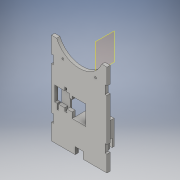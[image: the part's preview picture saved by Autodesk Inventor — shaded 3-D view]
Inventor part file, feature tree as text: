
AUTODESK INVENTOR PART (.ipt)
format: ipt  version: 2016 (Build 200138000, 138)  size: 343,552 bytes
history: native  units: in
note: dims shown in document units (in); Inventor stores cm internally (conversion verified against a paired STEP export)
features: reference x18, extrude x16, sketch x15, plane x2, projected_geometry x1
ambient origin geometry x8: Origin, YZ Plane, XZ Plane, XY Plane, X Axis, Y Axis, Z Axis, Center Point
bodies: Solid1 (feature_tree)
feature tree (52):
  extrude  "Extrusion1"  Depth=0.1969in TaperAngle=0.0deg
  extrude  "Extrusion2"  Depth=0.1969in TaperAngle=0.0deg
  extrude  "Extrusion3"  Depth=0.0787in
  extrude  "Extrusion4"  Depth=0.1969in TaperAngle=0.0deg
  extrude  "Extrusion6"  Depth=0.1969in
  extrude  "Extrusion7"  Depth=0.1969in TaperAngle=0.0deg
  extrude  "Extrusion8"  Depth=0.5in
  plane  "Work Plane1"
  extrude  "Extrusion18"  Depth=0.25in TaperAngle=0.0deg
  extrude  "Extrusion19"  Depth=0.15in
  extrude  "Extrusion21"  Depth=0.1181in
  plane  "Work Plane2"
  extrude  "Extrusion23"  Depth=1.0in TaperAngle=0.0deg
  extrude  "Extrusion24"  Depth=0.325in
  extrude  "Extrusion25"  Depth=0.0197in
  extrude  "Extrusion26"  Depth=0.0197in
  extrude  "Extrusion27"  Depth=1.0in
  extrude  "Extrusion28"  Depth=0.5in
  sketch  "Sketch1"  dims[d0=6.0in d1=0.1969in d2=0.0in]
  sketch  "Sketch2"  dims[d3=0.5906in d4=0.1969in d5=0.0in]
  reference  "Reference2"
  reference  "Reference3"
  sketch  "Sketch4"  dims[d6=3.0in d7=0.0787in]
  sketch  "Sketch6"  dims[d8=0.0787in d9=0.1969in d10=0.0in]
  sketch  "Sketch7"  dims[d11=0.1969in d12=0.1969in]
  sketch  "Sketch8"  dims[d13=0.1969in d14=0.1969in d15=0.0in]
  reference  "Reference6"
  reference  "Reference7"
  reference  "Reference8"
  reference  "Reference9"
  reference  "Reference10"
  reference  "Reference11"
  reference  "Reference12"
  reference  "Reference13"
  reference  "Reference14"
  reference  "Reference15"
  sketch  "Sketch18"  dims[d18=0.25in d19=0.5in]
  sketch  "Sketch20"  dims[d20=0.4in d21=0.0in d24=0.25in d25=0.0in]
  sketch  "Sketch22"  dims[d26=0.15in d27=0.1378in]
  sketch  "Sketch24"  dims[d28=0.0394in d29=0.1181in]
  reference  "Reference31"
  sketch  "Sketch25"  dims[d30=0.0394in d31=1.0in d32=0.0in]
  reference  "Reference32"
  reference  "Reference33"
  reference  "Reference34"
  sketch  "Sketch26"  dims[d33=0.02in d34=0.325in]
  reference  "Reference35"
  reference  "Reference36"
  sketch  "Sketch27"  dims[d35=0.02in d45=0.0197in]
  projected_geometry  "Projected Loop2"
  sketch  "Sketch28"  dims[d46=0.0197in d47=0.0197in]
  sketch  "Sketch29"  dims[d73=0.1181in d83=1.0in d84=0.5in d85=0.118in d86=1.0in d87=0.5in d88=0.118in d89=0.3937in d90=0.0in d91=0.8226in d92=0.0in d95=0.1in d96=0.0in d102=0.7in d103=1.063in d104=1.5in d106=0.7268in d107=0.8in d108=0.118in d109=0.5in d110=0.1in d111=1.2614in d112=0.0in d113=0.18in d114=0.18in d115=0.8in d116=0.3937in d117=0.0in d118=0.1181in d119=0.1181in d120=0.3937in d121=0.0in d122=0.0394in d123=0.0in d124=0.0394in d125=122.0in d126=0.0in d127=0.15in d128=122.0in d129=0.0in]
